# Revit family: Toilet-Floor_Mount-KOHLER-Reach-K-78080_1
name_source: partatom
category: Plumbing Fixtures
revit_build: Autodesk Revit 2015 (Build: 20140606_1530(x64)
units: mm (PartAtom-declared; Revit-internal decimal feet)

## types (6) — shared parameters
ADA Compliant = No
Assembly Code = D2010100
CW Connection = Yes
Cold Water Inlet = Cold Water Inlet
Date Modified = 6/1/2019
Default Elevation = 0"
Flow Rate = 0 GPM
Flush Rate- GPF = 1.28 GPF
Flush Rate- LPF = 4.8 LPF
HW Connection = No
Height = 29"
Hot Water Inlet = Hot Water Inlet
Length = 28 1/2"
Manufacturer = KOHLER Co.
MasterFormat 1995 = 15410
MasterFormat 2004 = 22.41.13
Material = Vitreous China
Pressure = 0.00 psi
Product Documentation Link = https://www.us.kohler.com
Product Name = Reach
Product Page URL = http://www.us.kohler.com
Rough-In = 12"
Seat Included = Yes
URL = https://www.us.kohler.com
Vent Connection = No
Waste Connection = Yes
Waste Water Outlet = Waste Water Outlet
WaterSense Certified = No
Width = 13 1/2"

## per-type parameters (varying)
| type | Description | Finish | Model | Right Hand Trip Lever | Type |
| Left Hand Trip Lever,0-White | One-piece elongated 1.28 gpf toilet with skirted trapway and left-hand trip lever | Kohler-Vitreous_China-0-White | K-78080-0 | No | 1 |
| Left Hand Trip Lever,7-Black Black | One-piece elongated 1.28 gpf toilet with skirted trapway and left-hand trip lever | Kohler-Vitreous_China-7-Black_Black | K-78080-7 | No | 2 |
| Left Hand Trip Lever,96-Biscuit | One-piece elongated 1.28 gpf toilet with skirted trapway and left-hand trip lever | Kohler-Vitreous_China-96-Biscuit | K-78080-96 | No | 3 |
| Left Hand Trip Lever,NY-Dune | One-piece elongated 1.28 gpf toilet with skirted trapway and left-hand trip lever | Kohler-Vitreous_China-NY-Dune | K-78080-NY | No | 4 |
| Right Hand Trip Lever,0-White | One-piece elongated 1.28 gpf toilet with skirted trapway and right-hand trip lever | Kohler-Vitreous_China-0-White | K-78080-RA-0 | Yes | 5 |
| Right Hand Trip Lever,96-Biscuit | One-piece elongated 1.28 gpf toilet with skirted trapway and right-hand trip lever | Kohler-Vitreous_China-96-Biscuit | K-78080-RA-96 | Yes | 6 |

## geometry (parser evidence)
native form markers: Sweep x5
no freeform markers — native parametric forms only
